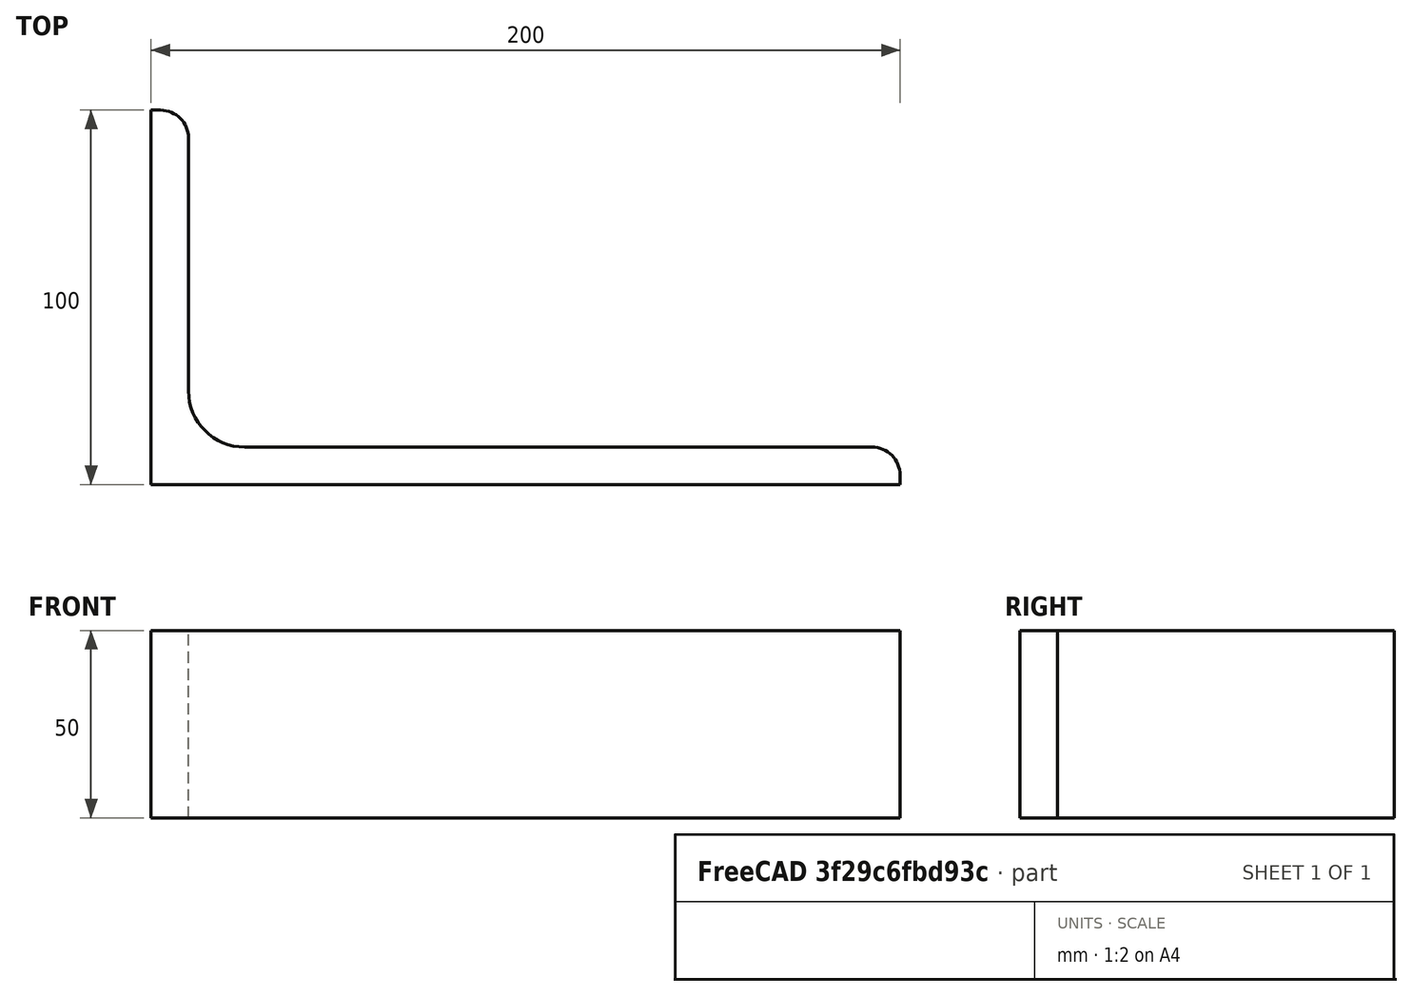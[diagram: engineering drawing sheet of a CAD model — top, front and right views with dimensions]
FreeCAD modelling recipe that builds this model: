
FCSTD DOCUMENT  (FreeCAD 0.15R4671 (Git))
Label: Angle Bar 200x100x10 EN10056 S235JR
License: All rights reserved
LicenseURL: http://en.wikipedia.org/wiki/All_rights_reserved
objects: Sketcher::SketchObject×1, Part::Extrusion×1
note: 2 computed .brp shape members not serialized (recipe doc carries the construction recipe); baked Part::Feature solids carry a one-line shape summary decoded from their .brp

FEATURE [Sketcher::SketchObject] Sketch
  sketch-geometry (9):
    g0: LineSegment StartX=0 StartY=0 StartZ=0 EndX=200 EndY=0 EndZ=0
    g1: LineSegment StartX=200 StartY=0 StartZ=0 EndX=200 EndY=2.5 EndZ=0
    g2: LineSegment StartX=192.5 StartY=10 StartZ=0 EndX=25 EndY=10 EndZ=0
    g3: LineSegment StartX=0 StartY=0 StartZ=0 EndX=0 EndY=100 EndZ=0
    g4: LineSegment StartX=0 StartY=100 StartZ=0 EndX=2.5 EndY=100 EndZ=0
    g5: LineSegment StartX=10 StartY=92.5 StartZ=0 EndX=10 EndY=25 EndZ=0
    g6: ArcOfCircle CenterX=25 CenterY=25 CenterZ=0 NormalX=0 NormalY=0 NormalZ=1 Radius=15 StartAngle=3.14159 EndAngle=4.71239
    g7: ArcOfCircle CenterX=2.5 CenterY=92.5 CenterZ=0 NormalX=0 NormalY=0 NormalZ=1 Radius=7.5 StartAngle=0 EndAngle=1.5708
    g8: ArcOfCircle CenterX=192.5 CenterY=2.5 CenterZ=0 NormalX=0 NormalY=0 NormalZ=1 Radius=7.5 StartAngle=0 EndAngle=1.5708
  constraints (23):
    c: Coincident(g0,g-1)
    c: Horizontal(g0)
    c: Coincident(g1,g0)
    c: Vertical(g1)
    c: Horizontal(g2)
    c: Coincident(g3,g-1)
    c: Vertical(g3)
    c: Coincident(g4,g3)
    c: Horizontal(g4)
    c: Vertical(g5)
    c: Tangent(g5,g6) = -1.5708
    c: Tangent(g2,g6) = 1.5708
    c: Tangent(g4,g7) = 1.5708
    c: Tangent(g5,g7) = 1.5708
    c: Tangent(g2,g8) = -1.5708
    c: Tangent(g1,g8) = -1.5708
    c: DistanceX(g0) = 200
    c: DistanceY(g3) = 100
    c: DistanceY(g0,g2) = 10
    c: DistanceX(g3,g5) = 10
    c: Radius(g6) = 15
    c: Radius(g8) = 7.5
    c: Radius(g7) = 7.5
FEATURE [Part::Extrusion] Extrude  label="Angle Bar 200x100x10 EN10056 S235JR"
  Base = -> Sketch
  Dir = (0,0,50)
  Solid = true
